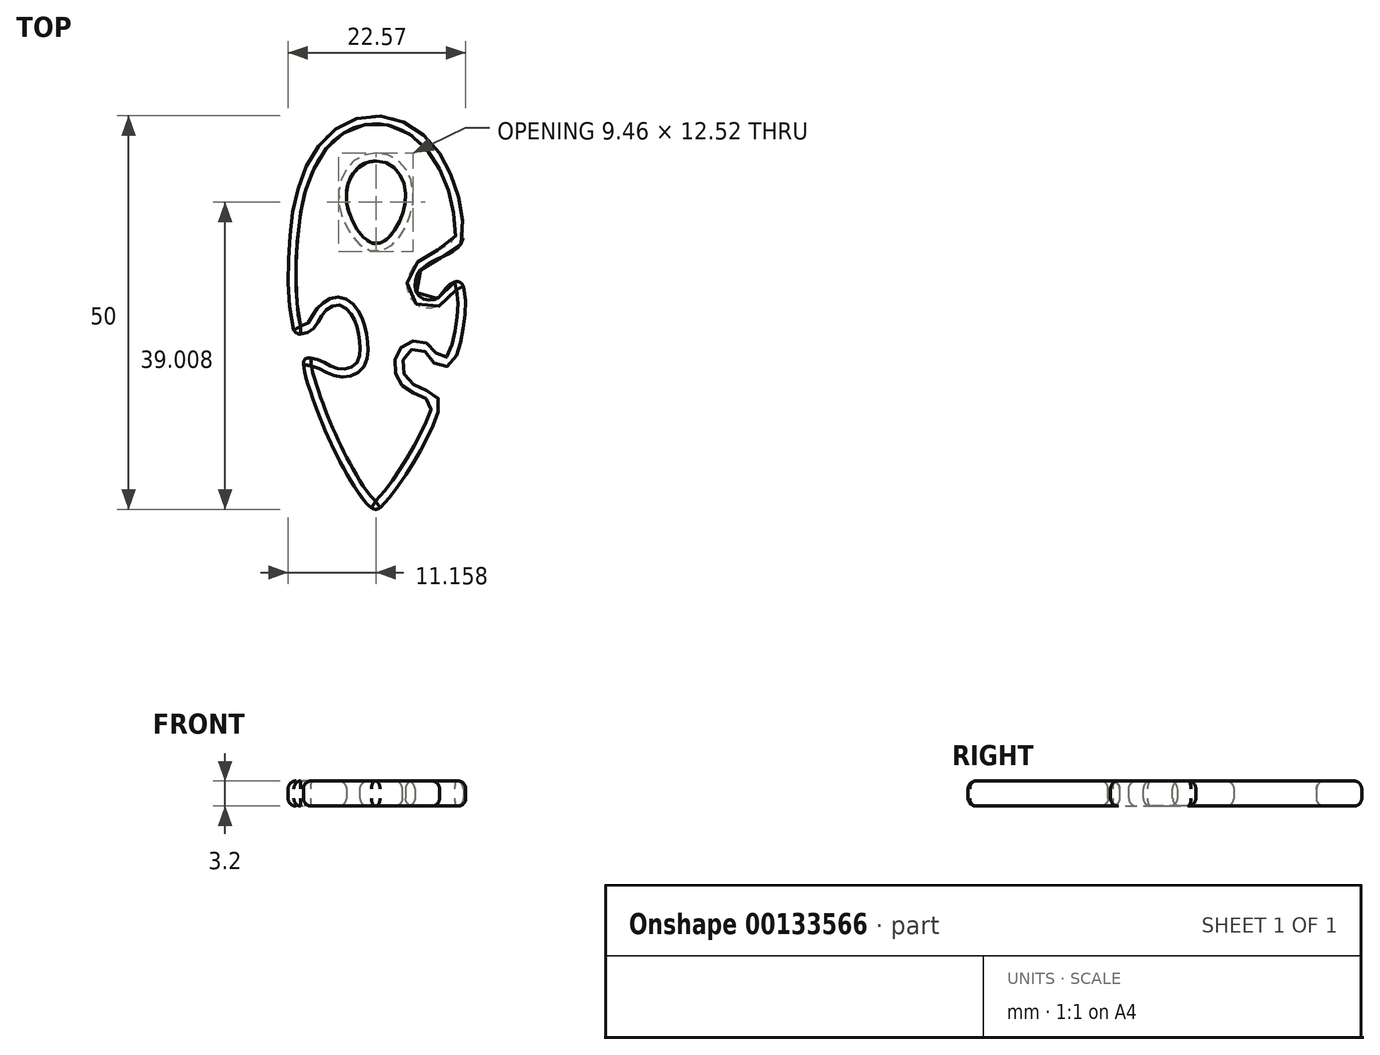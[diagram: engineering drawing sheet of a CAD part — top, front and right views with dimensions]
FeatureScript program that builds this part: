
annotation { "Feature Type Name" : "Feature", "Feature Type Description" : "" }
export const myFeature = defineFeature(function(context is Context, id is Id, definition is map)
    precondition{}
    {
        {
            var Q0;
            Q0=qCreatedBy(makeId("Top.planeOp"),FACE);
            var sketch = newSketch(context, id + "F0", { "sketchPlane" : qUnion([Q0])});
            skPoint(sketch, "E0.0.internal.snap0", {"position": v(0, 18.68) * mm});
            skFitSpline(sketch, "E1", {"points": [v(-0.01, 24.41) * mm, v(-5.78, 22.23) * mm, v(-10.07, 14.63) * mm, v(-11.18, 2.93) * mm, v(-10.85, -1.2) * mm, v(-10.07, -3.23) * mm, v(-8.06, -2.72) * mm, v(-6.87, -0.92) * mm, v(-4.9, 0.4) * mm, v(-3.01, -1.07) * mm, v(-2.09, -4.49) * mm, v(-2.5, -7.03) * mm, v(-4.52, -7.78) * mm, v(-7, -6.73) * mm, v(-9.01, -6.49) * mm, v(-8.8, -9.17) * mm, v(-5.68, -17.33) * mm, v(-1.64, -24.33) * mm, v(0, -25.59) * mm, v(1.43, -24.42) * mm, v(3.86, -21.08) * mm, v(7.46, -14.42) * mm, v(7.7, -11.24) * mm, v(3.99, -9.1) * mm, v(3.76, -5.86) * mm, v(5.78, -5.28) * mm, v(6.82, -6.38) * mm, v(7.7, -7.25) * mm, v(9.25, -7.32) * mm, v(11.05, -2.72) * mm, v(10.78, 3.18) * mm, v(9.08, 2.78) * mm, v(7.78, 1.22) * mm, v(5.45, 1.46) * mm, v(5.28, 4.32) * mm, v(8.31, 6.45) * mm, v(10.7, 8.04) * mm, v(11.06, 9.93) * mm, v(10.2, 14.99) * mm, v(6.2, 21.8) * mm, v(-0.01, 24.41) * mm]});
            skFitSpline(sketch, "E2", {"points": [v(0, 18.68) * mm, v(-2.35, 17.78) * mm, v(-3.71, 13.26) * mm, v(0, 8.16) * mm, v(3.65, 13.26) * mm, v(2.36, 17.78) * mm, v(0, 18.68) * mm]});
            skSolve(sketch);
        }
        {
            var Q0;
            Q0=makeQuery(id+"F0.imprint","IMPRINT",FACE,{"disambiguationData":[TD([[makeQuery(id+"F0.imprint","IMPRINT",EDGE,{"derivedFrom":sQuery(id+"F0.wireOp",EDGE,"E1")}),1.0]])]});
            extrude(context, id + "F1", {"entities" : qUnion([Q0]), "depth" : 3.2 * mm});
        }
        {
            var Q0;
            Q0=makeQuery(id+"F1.opExtrude","CAP_FACE",FACE,{"disambiguationData":[OSD([sQuery(id+"F0.wireOp",EDGE,"E1"),sQuery(id+"F0.wireOp",EDGE,"E2")])],"isStart":true});
            var Q1;
            Q1=makeQuery(id+"F1.opExtrude","CAP_FACE",FACE,{"disambiguationData":[OSD([sQuery(id+"F0.wireOp",EDGE,"E1"),sQuery(id+"F0.wireOp",EDGE,"E2")])],"isStart":false});
            fillet(context, id + "F2", {"entities" : qUnion([Q0, Q1]), "radius" : 1 * mm, "tangentPropagation" : true, "allowEdgeOverflow" : false});
        }
    });
